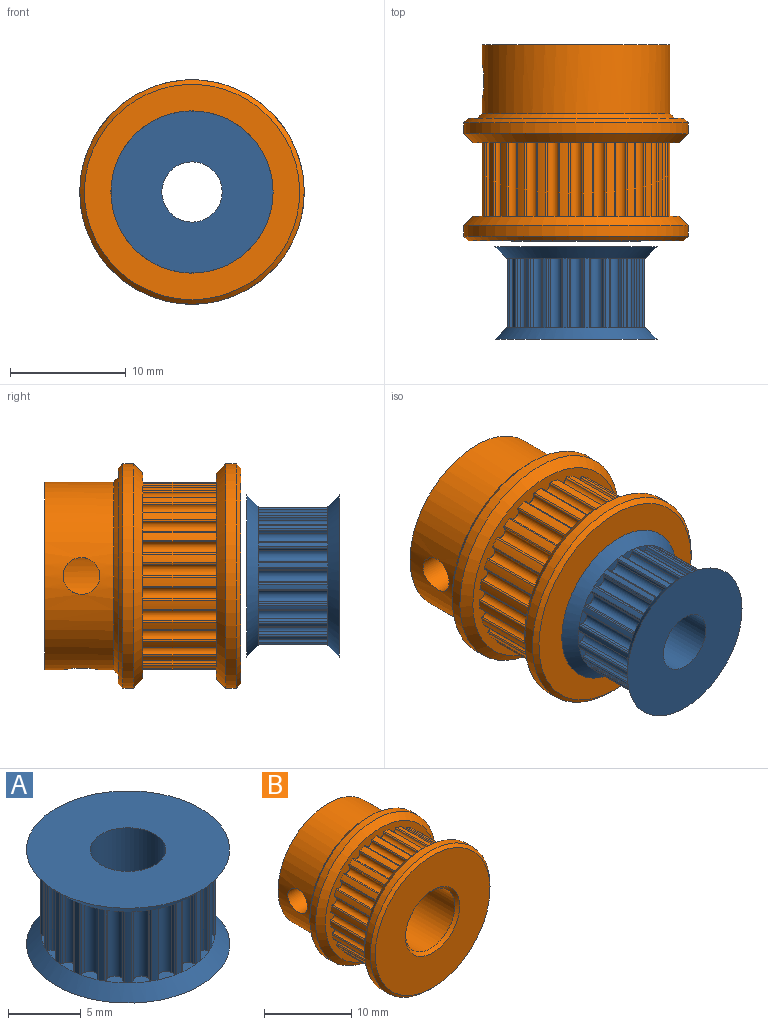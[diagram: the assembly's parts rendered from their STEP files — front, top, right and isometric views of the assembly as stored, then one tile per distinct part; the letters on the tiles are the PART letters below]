
ASSEMBLY  parts=2 mates=1
PART A: 165 faces, bbox 14x14x8 mm
  f0: plane 1.37x0.92mm, normal (0,0,1), area 0.7mm2, adj f65,f66,f67,f68,f69,f164
  f1: plane 1.44x0.75mm, normal (0,0,1), area 0.7mm2, adj f71,f72,f73,f74,f75,f164
  f2: plane 1.37x0.92mm, normal (0,0,1), area 0.7mm2, adj f77,f78,f79,f80,f81,f164
  f3: plane 1.23x1.1mm, normal (0,0,1), area 0.7mm2, adj f83,f84,f85,f86,f87,f164
  f4: plane 1.23x1.1mm, normal (0,0,1), area 0.7mm2, adj f89,f90,f91,f92,f93,f164
  f5: plane 1.37x0.92mm, normal (0,0,1), area 0.7mm2, adj f95,f96,f97,f98,f99,f164
  f6: plane 1.44x0.75mm, normal (0,0,1), area 0.7mm2, adj f101,f102,f103,f104,f105,f164
  f7: plane 1.37x0.92mm, normal (0,0,1), area 0.7mm2, adj f107,f108,f109,f110,f111,f164
  f8: plane 1.23x1.1mm, normal (0,0,1), area 0.7mm2, adj f113,f114,f115,f116,f117,f164
  f9: plane 1.23x1.1mm, normal (0,0,1), area 0.7mm2, adj f119,f120,f121,f122,f123,f164
  f10: plane 1.37x0.92mm, normal (0,0,1), area 0.7mm2, adj f125,f126,f127,f128,f129,f164
  f11: plane 1.44x0.75mm, normal (0,0,1), area 0.7mm2, adj f131,f132,f133,f134,f135,f164
  f12: plane 1.37x0.92mm, normal (0,0,1), area 0.7mm2, adj f137,f138,f139,f140,f141,f164
  f13: plane 1.23x1.1mm, normal (0,0,1), area 0.7mm2, adj f143,f144,f145,f146,f147,f164
  f14: plane 1.23x1.1mm, normal (0,0,1), area 0.7mm2, adj f149,f150,f151,f152,f153,f164
  f15: plane 1.37x0.92mm, normal (0,0,1), area 0.7mm2, adj f38,f39,f155,f156,f157,f164
  f16: plane 1.44x0.75mm, normal (0,0,1), area 0.7mm2, adj f41,f42,f43,f44,f45,f164
  f17: plane 1.37x0.92mm, normal (0,0,1), area 0.7mm2, adj f47,f48,f49,f50,f51,f164
  f18: plane 1.23x1.1mm, normal (0,0,1), area 0.7mm2, adj f53,f54,f55,f56,f57,f164
  f19: plane 1.23x1.1mm, normal (0,0,-1), area 0.7mm2, adj f59,f60,f61,f62,f63,f163
  f20: plane 1.23x1.1mm, normal (0,0,-1), area 0.7mm2, adj f53,f54,f55,f56,f57,f163
  f21: plane 1.37x0.92mm, normal (0,0,-1), area 0.7mm2, adj f47,f48,f49,f50,f51,f163
  f22: plane 1.44x0.75mm, normal (0,0,-1), area 0.7mm2, adj f41,f42,f43,f44,f45,f163
  f23: plane 1.37x0.92mm, normal (0,0,-1), area 0.7mm2, adj f38,f39,f155,f156,f157,f163
  f24: plane 1.23x1.1mm, normal (0,0,-1), area 0.7mm2, adj f149,f150,f151,f152,f153,f163
  f25: plane 1.23x1.1mm, normal (0,0,-1), area 0.7mm2, adj f143,f144,f145,f146,f147,f163
  f26: plane 1.37x0.92mm, normal (0,0,-1), area 0.7mm2, adj f137,f138,f139,f140,f141,f163
  f27: plane 1.44x0.75mm, normal (0,0,-1), area 0.7mm2, adj f131,f132,f133,f134,f135,f163
  f28: plane 1.37x0.92mm, normal (0,0,-1), area 0.7mm2, adj f125,f126,f127,f128,f129,f163
  f29: plane 1.23x1.1mm, normal (0,0,-1), area 0.7mm2, adj f119,f120,f121,f122,f123,f163
  f30: plane 1.23x1.1mm, normal (0,0,-1), area 0.7mm2, adj f113,f114,f115,f116,f117,f163
  f31: plane 1.37x0.92mm, normal (0,0,-1), area 0.7mm2, adj f107,f108,f109,f110,f111,f163
  f32: plane 1.44x0.75mm, normal (0,0,-1), area 0.7mm2, adj f101,f102,f103,f104,f105,f163
  f33: plane 1.37x0.92mm, normal (0,0,-1), area 0.7mm2, adj f95,f96,f97,f98,f99,f163
  f34: plane 1.23x1.1mm, normal (0,0,-1), area 0.7mm2, adj f89,f90,f91,f92,f93,f163
  f35: plane 1.23x1.1mm, normal (0,0,-1), area 0.7mm2, adj f83,f84,f85,f86,f87,f163
  f36: plane 1.37x0.92mm, normal (0,0,-1), area 0.7mm2, adj f77,f78,f79,f80,f81,f163
  f37: plane 1.44x0.75mm, normal (0,0,-1), area 0.7mm2, adj f71,f72,f73,f74,f75,f163
  f38: cylinder r=1mm len=6mm, axis (0,0,-1), area 1.5mm2, adj f15,f23,f39,f157
  f39: cylinder r=0.15mm len=6mm, axis (0,0,-1), area 1.1mm2, adj f15,f23,f38,f40
  f40: cylinder r=6mm len=6mm, axis (0,0,-1), area 2.7mm2, adj f39,f41,f163,f164
  f41: cylinder r=0.15mm len=6mm, axis (0,0,-1), area 1.1mm2, adj f16,f22,f40,f42
  f42: cylinder r=1mm len=6mm, axis (0,0,-1), area 1.5mm2, adj f16,f22,f41,f43
  f43: cylinder r=0.56mm len=6mm, axis (0,0,-1), area 7.9mm2, adj f16,f22,f42,f44
  f44: cylinder r=1mm len=6mm, axis (0,0,-1), area 1.5mm2, adj f16,f22,f43,f45
  f45: cylinder r=0.15mm len=6mm, axis (0,0,-1), area 1.1mm2, adj f16,f22,f44,f46
  f46: cylinder r=6mm len=6mm, axis (0,0,-1), area 2.7mm2, adj f45,f47,f163,f164
  f47: cylinder r=0.15mm len=6mm, axis (0,0,-1), area 1.1mm2, adj f17,f21,f46,f48
  f48: cylinder r=1mm len=6mm, axis (0,0,-1), area 1.5mm2, adj f17,f21,f47,f49
  f49: cylinder r=0.56mm len=6mm, axis (0,0,-1), area 7.9mm2, adj f17,f21,f48,f50
  f50: cylinder r=1mm len=6mm, axis (0,0,-1), area 1.5mm2, adj f17,f21,f49,f51
  f51: cylinder r=0.15mm len=6mm, axis (0,0,-1), area 1.1mm2, adj f17,f21,f50,f52
  f52: cylinder r=6mm len=6mm, axis (0,0,-1), area 2.7mm2, adj f51,f53,f163,f164
  f53: cylinder r=0.15mm len=6mm, axis (0,0,-1), area 1.1mm2, adj f18,f20,f52,f54
  f54: cylinder r=1mm len=6mm, axis (0,0,-1), area 1.5mm2, adj f18,f20,f53,f55
  f55: cylinder r=0.56mm len=6mm, axis (0,0,-1), area 7.9mm2, adj f18,f20,f54,f56
  f56: cylinder r=1mm len=6mm, axis (0,0,-1), area 1.5mm2, adj f18,f20,f55,f57
  f57: cylinder r=0.15mm len=6mm, axis (0,0,-1), area 1.1mm2, adj f18,f20,f56,f58
  f58: cylinder r=6mm len=6mm, axis (0,0,-1), area 2.7mm2, adj f57,f59,f163,f164
  f59: cylinder r=0.15mm len=6mm, axis (0,0,-1), area 1.1mm2, adj f19,f58,f60,f160
  f60: cylinder r=1mm len=6mm, axis (0,0,-1), area 1.5mm2, adj f19,f59,f61,f160
  f61: cylinder r=0.56mm len=6mm, axis (0,0,-1), area 7.9mm2, adj f19,f60,f62,f160
  f62: cylinder r=1mm len=6mm, axis (0,0,-1), area 1.5mm2, adj f19,f61,f63,f160
  f63: cylinder r=0.15mm len=6mm, axis (0,0,-1), area 1.1mm2, adj f19,f62,f64,f160
  f64: cylinder r=6mm len=6mm, axis (0,0,-1), area 2.2mm2, adj f63,f65,f163,f164
  f65: cylinder r=0.15mm len=6mm, axis (0,0,-1), area 1.6mm2, adj f0,f64,f66,f158,f163,f164
  f66: cylinder r=1mm len=6mm, axis (0,0,-1), area 1.5mm2, adj f0,f65,f67,f158
  f67: cylinder r=0.56mm len=6mm, axis (0,0,-1), area 7.9mm2, adj f0,f66,f68,f158
  f68: cylinder r=1mm len=6mm, axis (0,0,-1), area 1.5mm2, adj f0,f67,f69,f158
  f69: cylinder r=0.15mm len=6mm, axis (0,0,-1), area 1.1mm2, adj f0,f68,f70,f158
  f70: cylinder r=6mm len=6mm, axis (0,0,-1), area 2.7mm2, adj f69,f71,f163,f164
  f71: cylinder r=0.15mm len=6mm, axis (0,0,-1), area 1.1mm2, adj f1,f37,f70,f72
  f72: cylinder r=1mm len=6mm, axis (0,0,-1), area 1.5mm2, adj f1,f37,f71,f73
  f73: cylinder r=0.56mm len=6mm, axis (0,0,-1), area 7.9mm2, adj f1,f37,f72,f74
  f74: cylinder r=1mm len=6mm, axis (0,0,-1), area 1.5mm2, adj f1,f37,f73,f75
  f75: cylinder r=0.15mm len=6mm, axis (0,0,-1), area 1.1mm2, adj f1,f37,f74,f76
  f76: cylinder r=6mm len=6mm, axis (0,0,-1), area 2.7mm2, adj f75,f77,f163,f164
  f77: cylinder r=0.15mm len=6mm, axis (0,0,-1), area 1.1mm2, adj f2,f36,f76,f78
  f78: cylinder r=1mm len=6mm, axis (0,0,-1), area 1.5mm2, adj f2,f36,f77,f79
  f79: cylinder r=0.56mm len=6mm, axis (0,0,-1), area 7.9mm2, adj f2,f36,f78,f80
  f80: cylinder r=1mm len=6mm, axis (0,0,-1), area 1.5mm2, adj f2,f36,f79,f81
  f81: cylinder r=0.15mm len=6mm, axis (0,0,-1), area 1.1mm2, adj f2,f36,f80,f82
  f82: cylinder r=6mm len=6mm, axis (0,0,-1), area 2.7mm2, adj f81,f83,f163,f164
  f83: cylinder r=0.15mm len=6mm, axis (0,0,-1), area 1.1mm2, adj f3,f35,f82,f84
  f84: cylinder r=1mm len=6mm, axis (0,0,-1), area 1.5mm2, adj f3,f35,f83,f85
  f85: cylinder r=0.56mm len=6mm, axis (0,0,-1), area 7.9mm2, adj f3,f35,f84,f86
  f86: cylinder r=1mm len=6mm, axis (0,0,-1), area 1.5mm2, adj f3,f35,f85,f87
  f87: cylinder r=0.15mm len=6mm, axis (0,0,-1), area 1.1mm2, adj f3,f35,f86,f88
  f88: cylinder r=6mm len=6mm, axis (0,0,-1), area 2.7mm2, adj f87,f89,f163,f164
  f89: cylinder r=0.15mm len=6mm, axis (0,0,-1), area 1.1mm2, adj f4,f34,f88,f90
  f90: cylinder r=1mm len=6mm, axis (0,0,-1), area 1.5mm2, adj f4,f34,f89,f91
  f91: cylinder r=0.56mm len=6mm, axis (0,0,-1), area 7.9mm2, adj f4,f34,f90,f92
  f92: cylinder r=1mm len=6mm, axis (0,0,-1), area 1.5mm2, adj f4,f34,f91,f93
  f93: cylinder r=0.15mm len=6mm, axis (0,0,-1), area 1.1mm2, adj f4,f34,f92,f94
  f94: cylinder r=6mm len=6mm, axis (0,0,-1), area 2.7mm2, adj f93,f95,f163,f164
  f95: cylinder r=0.15mm len=6mm, axis (0,0,-1), area 1.1mm2, adj f5,f33,f94,f96
  f96: cylinder r=1mm len=6mm, axis (0,0,-1), area 1.5mm2, adj f5,f33,f95,f97
  f97: cylinder r=0.56mm len=6mm, axis (0,0,-1), area 7.9mm2, adj f5,f33,f96,f98
  f98: cylinder r=1mm len=6mm, axis (0,0,-1), area 1.5mm2, adj f5,f33,f97,f99
  f99: cylinder r=0.15mm len=6mm, axis (0,0,-1), area 1.1mm2, adj f5,f33,f98,f100
  f100: cylinder r=6mm len=6mm, axis (0,0,-1), area 2.7mm2, adj f99,f101,f163,f164
  f101: cylinder r=0.15mm len=6mm, axis (0,0,-1), area 1.1mm2, adj f6,f32,f100,f102
  f102: cylinder r=1mm len=6mm, axis (0,0,-1), area 1.5mm2, adj f6,f32,f101,f103
  f103: cylinder r=0.56mm len=6mm, axis (0,0,-1), area 7.9mm2, adj f6,f32,f102,f104
  f104: cylinder r=1mm len=6mm, axis (0,0,-1), area 1.5mm2, adj f6,f32,f103,f105
  f105: cylinder r=0.15mm len=6mm, axis (0,0,-1), area 1.1mm2, adj f6,f32,f104,f106
  f106: cylinder r=6mm len=6mm, axis (0,0,-1), area 2.7mm2, adj f105,f107,f163,f164
  f107: cylinder r=0.15mm len=6mm, axis (0,0,-1), area 1.1mm2, adj f7,f31,f106,f108
  f108: cylinder r=1mm len=6mm, axis (0,0,-1), area 1.5mm2, adj f7,f31,f107,f109
  f109: cylinder r=0.56mm len=6mm, axis (0,0,-1), area 7.9mm2, adj f7,f31,f108,f110
  f110: cylinder r=1mm len=6mm, axis (0,0,-1), area 1.5mm2, adj f7,f31,f109,f111
  f111: cylinder r=0.15mm len=6mm, axis (0,0,-1), area 1.1mm2, adj f7,f31,f110,f112
  f112: cylinder r=6mm len=6mm, axis (0,0,-1), area 2.7mm2, adj f111,f113,f163,f164
  f113: cylinder r=0.15mm len=6mm, axis (0,0,-1), area 1.1mm2, adj f8,f30,f112,f114
  f114: cylinder r=1mm len=6mm, axis (0,0,-1), area 1.5mm2, adj f8,f30,f113,f115
  f115: cylinder r=0.56mm len=6mm, axis (0,0,-1), area 7.9mm2, adj f8,f30,f114,f116
  f116: cylinder r=1mm len=6mm, axis (0,0,-1), area 1.5mm2, adj f8,f30,f115,f117
  f117: cylinder r=0.15mm len=6mm, axis (0,0,-1), area 1.1mm2, adj f8,f30,f116,f118
  f118: cylinder r=6mm len=6mm, axis (0,0,-1), area 2.7mm2, adj f117,f119,f163,f164
  f119: cylinder r=0.15mm len=6mm, axis (0,0,-1), area 1.1mm2, adj f9,f29,f118,f120
  f120: cylinder r=1mm len=6mm, axis (0,0,-1), area 1.5mm2, adj f9,f29,f119,f121
  f121: cylinder r=0.56mm len=6mm, axis (0,0,-1), area 7.9mm2, adj f9,f29,f120,f122
  f122: cylinder r=1mm len=6mm, axis (0,0,-1), area 1.5mm2, adj f9,f29,f121,f123
  f123: cylinder r=0.15mm len=6mm, axis (0,0,-1), area 1.1mm2, adj f9,f29,f122,f124
  f124: cylinder r=6mm len=6mm, axis (0,0,-1), area 2.7mm2, adj f123,f125,f163,f164
  f125: cylinder r=0.15mm len=6mm, axis (0,0,-1), area 1.1mm2, adj f10,f28,f124,f126
  f126: cylinder r=1mm len=6mm, axis (0,0,-1), area 1.5mm2, adj f10,f28,f125,f127
  f127: cylinder r=0.56mm len=6mm, axis (0,0,-1), area 7.9mm2, adj f10,f28,f126,f128
  f128: cylinder r=1mm len=6mm, axis (0,0,-1), area 1.5mm2, adj f10,f28,f127,f129
  f129: cylinder r=0.15mm len=6mm, axis (0,0,-1), area 1.1mm2, adj f10,f28,f128,f130
  f130: cylinder r=6mm len=6mm, axis (0,0,-1), area 2.7mm2, adj f129,f131,f163,f164
  f131: cylinder r=0.15mm len=6mm, axis (0,0,-1), area 1.1mm2, adj f11,f27,f130,f132
  f132: cylinder r=1mm len=6mm, axis (0,0,-1), area 1.5mm2, adj f11,f27,f131,f133
  f133: cylinder r=0.56mm len=6mm, axis (0,0,-1), area 7.9mm2, adj f11,f27,f132,f134
  f134: cylinder r=1mm len=6mm, axis (0,0,-1), area 1.5mm2, adj f11,f27,f133,f135
  f135: cylinder r=0.15mm len=6mm, axis (0,0,-1), area 1.1mm2, adj f11,f27,f134,f136
  f136: cylinder r=6mm len=6mm, axis (0,0,-1), area 2.7mm2, adj f135,f137,f163,f164
  f137: cylinder r=0.15mm len=6mm, axis (0,0,-1), area 1.1mm2, adj f12,f26,f136,f138
  f138: cylinder r=1mm len=6mm, axis (0,0,-1), area 1.5mm2, adj f12,f26,f137,f139
  f139: cylinder r=0.56mm len=6mm, axis (0,0,-1), area 7.9mm2, adj f12,f26,f138,f140
  f140: cylinder r=1mm len=6mm, axis (0,0,-1), area 1.5mm2, adj f12,f26,f139,f141
  f141: cylinder r=0.15mm len=6mm, axis (0,0,-1), area 1.1mm2, adj f12,f26,f140,f142
  f142: cylinder r=6mm len=6mm, axis (0,0,-1), area 2.7mm2, adj f141,f143,f163,f164
  f143: cylinder r=0.15mm len=6mm, axis (0,0,-1), area 1.1mm2, adj f13,f25,f142,f144
  f144: cylinder r=1mm len=6mm, axis (0,0,-1), area 1.5mm2, adj f13,f25,f143,f145
  f145: cylinder r=0.56mm len=6mm, axis (0,0,-1), area 7.9mm2, adj f13,f25,f144,f146
  f146: cylinder r=1mm len=6mm, axis (0,0,-1), area 1.5mm2, adj f13,f25,f145,f147
  f147: cylinder r=0.15mm len=6mm, axis (0,0,-1), area 1.1mm2, adj f13,f25,f146,f148
  f148: cylinder r=6mm len=6mm, axis (0,0,-1), area 2.7mm2, adj f147,f149,f163,f164
  f149: cylinder r=0.15mm len=6mm, axis (0,0,-1), area 1.1mm2, adj f14,f24,f148,f150
  f150: cylinder r=1mm len=6mm, axis (0,0,-1), area 1.5mm2, adj f14,f24,f149,f151
  f151: cylinder r=0.56mm len=6mm, axis (0,0,-1), area 7.9mm2, adj f14,f24,f150,f152
  f152: cylinder r=1mm len=6mm, axis (0,0,-1), area 1.5mm2, adj f14,f24,f151,f153
  f153: cylinder r=0.15mm len=6mm, axis (0,0,-1), area 1.1mm2, adj f14,f24,f152,f154
  f154: cylinder r=6mm len=6mm, axis (0,0,-1), area 2.7mm2, adj f153,f155,f163,f164
  f155: cylinder r=0.15mm len=6mm, axis (0,0,-1), area 1.1mm2, adj f15,f23,f154,f156
  f156: cylinder r=1mm len=6mm, axis (0,0,-1), area 1.5mm2, adj f15,f23,f155,f157
  f157: cylinder r=0.56mm len=6mm, axis (0,0,-1), area 7.9mm2, adj f15,f23,f38,f156
  f158: plane 1.37x0.92mm, normal (0,0,-1), area 0.7mm2, adj f65,f66,f67,f68,f69,f163
  f159: plane 14x14mm, normal (0,0,1), area 132.7mm2, adj f162,f163
  f160: plane 1.23x1.1mm, normal (0,0,1), area 0.7mm2, adj f59,f60,f61,f62,f63,f164
  f161: plane 14x14mm, normal (0,0,-1), area 132.7mm2, adj f162,f164
  f162: cylinder r=2.6mm len=8mm, axis (0,0,-1), area 130.7mm2, adj f159,f161
  f163: cone r=7mm half-angle=45deg, axis (0,0,1), area 57.8mm2, adj f19,f20,f21,f22,f23,f24,f25,f26
  f164: cone r=7mm half-angle=45deg, axis (0,0,-1), area 57.8mm2, adj f0,f1,f2,f3,f4,f5,f6,f7
PART B: 117 faces, bbox 19.4x16.9x19.4 mm
  f0: cylinder r=8.1mm len=16.21mm, axis (0,-1,0), area 287.2mm2, adj f1,f108,f114,f116
  f1: cylinder r=1.59mm len=4.43mm, axis (1,0,0), area 41.8mm2, adj f0,f109
  f2: cylinder r=0.5mm len=6.35mm, axis (0,1,0), area 9.8mm2, adj f3,f101,f102,f105
  f3: cylinder r=0.12mm len=6.35mm, axis (0,1,0), area 1.3mm2, adj f2,f4,f102,f105
  f4: cylinder r=8.1mm len=6.35mm, axis (0,1,0), area 4.9mm2, adj f3,f5,f102,f105
  f5: cylinder r=0.12mm len=6.35mm, axis (0,1,0), area 1.3mm2, adj f4,f6,f102,f105
  f6: cylinder r=0.5mm len=6.35mm, axis (0,1,0), area 9.8mm2, adj f5,f7,f102,f105
  f7: cylinder r=0.12mm len=6.35mm, axis (0,1,0), area 1.3mm2, adj f6,f8,f102,f105
  f8: cylinder r=8.1mm len=6.35mm, axis (0,1,0), area 4.9mm2, adj f7,f9,f102,f105
  f9: cylinder r=0.12mm len=6.35mm, axis (0,1,0), area 1.3mm2, adj f8,f10,f102,f105
  f10: cylinder r=0.5mm len=6.35mm, axis (0,1,0), area 9.8mm2, adj f9,f11,f102,f105
  f11: cylinder r=0.12mm len=6.35mm, axis (0,1,0), area 1.3mm2, adj f10,f12,f102,f105
  f12: cylinder r=8.1mm len=6.35mm, axis (0,1,0), area 4.9mm2, adj f11,f13,f102,f105
  f13: cylinder r=0.12mm len=6.35mm, axis (0,1,0), area 1.3mm2, adj f12,f14,f102,f105
  f14: cylinder r=0.5mm len=6.35mm, axis (0,1,0), area 9.8mm2, adj f13,f15,f102,f105
  f15: cylinder r=0.12mm len=6.35mm, axis (0,1,0), area 1.3mm2, adj f14,f16,f102,f105
  f16: cylinder r=8.1mm len=6.35mm, axis (0,1,0), area 4.9mm2, adj f15,f17,f102,f105
  f17: cylinder r=0.12mm len=6.35mm, axis (0,1,0), area 1.3mm2, adj f16,f18,f102,f105
  f18: cylinder r=0.5mm len=6.35mm, axis (0,1,0), area 9.8mm2, adj f17,f19,f102,f105
  f19: cylinder r=0.12mm len=6.35mm, axis (0,1,0), area 1.3mm2, adj f18,f20,f102,f105
  f20: cylinder r=8.1mm len=6.35mm, axis (0,1,0), area 4.9mm2, adj f19,f21,f102,f105
  f21: cylinder r=0.12mm len=6.35mm, axis (0,1,0), area 1.3mm2, adj f20,f22,f102,f105
  f22: cylinder r=0.5mm len=6.35mm, axis (0,1,0), area 9.8mm2, adj f21,f23,f102,f105
  f23: cylinder r=0.12mm len=6.35mm, axis (0,1,0), area 1.3mm2, adj f22,f24,f102,f105
  f24: cylinder r=8.1mm len=6.35mm, axis (0,1,0), area 4.9mm2, adj f23,f25,f102,f105
  f25: cylinder r=0.12mm len=6.35mm, axis (0,1,0), area 1.3mm2, adj f24,f26,f102,f105
  f26: cylinder r=0.5mm len=6.35mm, axis (0,1,0), area 9.8mm2, adj f25,f27,f102,f105
  f27: cylinder r=0.12mm len=6.35mm, axis (0,1,0), area 1.3mm2, adj f26,f28,f102,f105
  f28: cylinder r=8.1mm len=6.35mm, axis (0,1,0), area 4.9mm2, adj f27,f29,f102,f105
  f29: cylinder r=0.12mm len=6.35mm, axis (0,1,0), area 1.3mm2, adj f28,f30,f102,f105
  f30: cylinder r=0.5mm len=6.35mm, axis (0,1,0), area 9.8mm2, adj f29,f31,f102,f105
  f31: cylinder r=0.12mm len=6.35mm, axis (0,1,0), area 1.3mm2, adj f30,f32,f102,f105
  f32: cylinder r=8.1mm len=6.35mm, axis (0,1,0), area 4.9mm2, adj f31,f33,f102,f105
  f33: cylinder r=0.12mm len=6.35mm, axis (0,1,0), area 1.3mm2, adj f32,f34,f102,f105
  f34: cylinder r=0.5mm len=6.35mm, axis (0,1,0), area 9.8mm2, adj f33,f35,f102,f105
  f35: cylinder r=0.12mm len=6.35mm, axis (0,1,0), area 1.3mm2, adj f34,f36,f102,f105
  f36: cylinder r=8.1mm len=6.35mm, axis (0,1,0), area 4.9mm2, adj f35,f37,f102,f105
  f37: cylinder r=0.12mm len=6.35mm, axis (0,1,0), area 1.3mm2, adj f36,f38,f102,f105
  f38: cylinder r=0.5mm len=6.35mm, axis (0,1,0), area 9.8mm2, adj f37,f39,f102,f105
  f39: cylinder r=0.12mm len=6.35mm, axis (0,1,0), area 1.3mm2, adj f38,f40,f102,f105
  f40: cylinder r=8.1mm len=6.35mm, axis (0,1,0), area 4.9mm2, adj f39,f41,f102,f105
  f41: cylinder r=0.12mm len=6.35mm, axis (0,1,0), area 1.3mm2, adj f40,f42,f102,f105
  f42: cylinder r=0.5mm len=6.35mm, axis (0,1,0), area 9.8mm2, adj f41,f43,f102,f105
  f43: cylinder r=0.12mm len=6.35mm, axis (0,1,0), area 1.3mm2, adj f42,f44,f102,f105
  f44: cylinder r=8.1mm len=6.35mm, axis (0,1,0), area 4.9mm2, adj f43,f45,f102,f105
  f45: cylinder r=0.12mm len=6.35mm, axis (0,1,0), area 1.3mm2, adj f44,f46,f102,f105
  f46: cylinder r=0.5mm len=6.35mm, axis (0,1,0), area 9.8mm2, adj f45,f47,f102,f105
  f47: cylinder r=0.12mm len=6.35mm, axis (0,1,0), area 1.3mm2, adj f46,f48,f102,f105
  f48: cylinder r=8.1mm len=6.35mm, axis (0,1,0), area 4.9mm2, adj f47,f49,f102,f105
  f49: cylinder r=0.12mm len=6.35mm, axis (0,1,0), area 1.3mm2, adj f48,f50,f102,f105
  f50: cylinder r=0.5mm len=6.35mm, axis (0,1,0), area 9.8mm2, adj f49,f51,f102,f105
  f51: cylinder r=0.12mm len=6.35mm, axis (0,1,0), area 1.3mm2, adj f50,f52,f102,f105
  f52: cylinder r=8.1mm len=6.35mm, axis (0,1,0), area 4.9mm2, adj f51,f53,f102,f105
  f53: cylinder r=0.12mm len=6.35mm, axis (0,1,0), area 1.3mm2, adj f52,f54,f102,f105
  f54: cylinder r=0.5mm len=6.35mm, axis (0,1,0), area 9.8mm2, adj f53,f55,f102,f105
  f55: cylinder r=0.12mm len=6.35mm, axis (0,1,0), area 1.3mm2, adj f54,f56,f102,f105
  f56: cylinder r=8.1mm len=6.35mm, axis (0,1,0), area 4.9mm2, adj f55,f57,f102,f105
  f57: cylinder r=0.12mm len=6.35mm, axis (0,1,0), area 1.3mm2, adj f56,f58,f102,f105
  f58: cylinder r=0.5mm len=6.35mm, axis (0,1,0), area 9.8mm2, adj f57,f59,f102,f105
  f59: cylinder r=0.12mm len=6.35mm, axis (0,1,0), area 1.3mm2, adj f58,f60,f102,f105
  f60: cylinder r=8.1mm len=6.35mm, axis (0,1,0), area 4.9mm2, adj f59,f61,f102,f105
  f61: cylinder r=0.12mm len=6.35mm, axis (0,1,0), area 1.3mm2, adj f60,f62,f102,f105
  f62: cylinder r=0.5mm len=6.35mm, axis (0,1,0), area 9.8mm2, adj f61,f63,f102,f105
  f63: cylinder r=0.12mm len=6.35mm, axis (0,1,0), area 1.3mm2, adj f62,f64,f102,f105
  f64: cylinder r=8.1mm len=6.35mm, axis (0,1,0), area 4.9mm2, adj f63,f65,f102,f105
  f65: cylinder r=0.12mm len=6.35mm, axis (0,1,0), area 1.3mm2, adj f64,f66,f102,f105
  f66: cylinder r=0.5mm len=6.35mm, axis (0,1,0), area 9.8mm2, adj f65,f67,f102,f105
  f67: cylinder r=0.12mm len=6.35mm, axis (0,1,0), area 1.3mm2, adj f66,f68,f102,f105
  f68: cylinder r=8.1mm len=6.35mm, axis (0,1,0), area 4.9mm2, adj f67,f69,f102,f105
  f69: cylinder r=0.12mm len=6.35mm, axis (0,1,0), area 1.3mm2, adj f68,f70,f102,f105
  f70: cylinder r=0.5mm len=6.35mm, axis (0,1,0), area 9.8mm2, adj f69,f71,f102,f105
  f71: cylinder r=0.12mm len=6.35mm, axis (0,1,0), area 1.3mm2, adj f70,f72,f102,f105
  f72: cylinder r=8.1mm len=6.35mm, axis (0,1,0), area 4.9mm2, adj f71,f73,f102,f105
  f73: cylinder r=0.12mm len=6.35mm, axis (0,1,0), area 1.3mm2, adj f72,f74,f102,f105
  f74: cylinder r=0.5mm len=6.35mm, axis (0,1,0), area 9.8mm2, adj f73,f75,f102,f105
  f75: cylinder r=0.12mm len=6.35mm, axis (0,1,0), area 1.3mm2, adj f74,f76,f102,f105
  f76: cylinder r=8.1mm len=6.35mm, axis (0,1,0), area 4.9mm2, adj f75,f77,f102,f105
  f77: cylinder r=0.12mm len=6.35mm, axis (0,1,0), area 1.3mm2, adj f76,f78,f102,f105
  f78: cylinder r=0.5mm len=6.35mm, axis (0,1,0), area 9.8mm2, adj f77,f79,f102,f105
  f79: cylinder r=0.12mm len=6.35mm, axis (0,1,0), area 1.3mm2, adj f78,f80,f102,f105
  f80: cylinder r=8.1mm len=6.35mm, axis (0,1,0), area 4.9mm2, adj f79,f81,f102,f105
  f81: cylinder r=0.12mm len=6.35mm, axis (0,1,0), area 1.3mm2, adj f80,f82,f102,f105
  f82: cylinder r=0.5mm len=6.35mm, axis (0,1,0), area 9.8mm2, adj f81,f83,f102,f105
  f83: cylinder r=0.12mm len=6.35mm, axis (0,1,0), area 1.3mm2, adj f82,f84,f102,f105
  f84: cylinder r=8.1mm len=6.35mm, axis (0,1,0), area 4.9mm2, adj f83,f85,f102,f105
  f85: cylinder r=0.12mm len=6.35mm, axis (0,1,0), area 1.3mm2, adj f84,f86,f102,f105
  f86: cylinder r=0.5mm len=6.35mm, axis (0,1,0), area 9.8mm2, adj f85,f87,f102,f105
  f87: cylinder r=0.12mm len=6.35mm, axis (0,1,0), area 1.3mm2, adj f86,f88,f102,f105
  f88: cylinder r=8.1mm len=6.35mm, axis (0,1,0), area 4.9mm2, adj f87,f89,f102,f105
  f89: cylinder r=0.12mm len=6.35mm, axis (0,1,0), area 1.3mm2, adj f88,f90,f102,f105
  f90: cylinder r=0.5mm len=6.35mm, axis (0,1,0), area 9.8mm2, adj f89,f91,f102,f105
  f91: cylinder r=0.12mm len=6.35mm, axis (0,1,0), area 1.3mm2, adj f90,f92,f102,f105
  f92: cylinder r=8.1mm len=6.35mm, axis (0,1,0), area 4.9mm2, adj f91,f93,f102,f105
  f93: cylinder r=0.12mm len=6.35mm, axis (0,1,0), area 1.3mm2, adj f92,f94,f102,f105
  f94: cylinder r=0.5mm len=6.35mm, axis (0,1,0), area 9.8mm2, adj f93,f95,f102,f105
  f95: cylinder r=0.12mm len=6.35mm, axis (0,1,0), area 1.3mm2, adj f94,f96,f102,f105
  f96: cylinder r=8.1mm len=6.35mm, axis (0,1,0), area 4.9mm2, adj f95,f97,f102,f105
  f97: cylinder r=0.12mm len=6.35mm, axis (0,1,0), area 1.3mm2, adj f96,f98,f102,f105
  f98: cylinder r=0.5mm len=6.35mm, axis (0,1,0), area 9.8mm2, adj f97,f99,f102,f105
  f99: cylinder r=0.12mm len=6.35mm, axis (0,1,0), area 1.3mm2, adj f98,f100,f102,f105
  f100: cylinder r=8.1mm len=6.35mm, axis (0,1,0), area 4.9mm2, adj f99,f101,f102,f105
  f101: cylinder r=0.12mm len=6.35mm, axis (0,1,0), area 1.3mm2, adj f2,f100,f102,f105
  f102: plane 17.8x17.8mm, normal (0,-1,0), area 55.4mm2, adj f2,f3,f4,f5,f6,f7,f8,f9
  f103: cylinder r=9.69mm len=19.38mm, axis (0,-1,0), area 56.4mm2, adj f110,f115
  f104: plane 18.59x18.59mm, normal (0,1,0), area 44.4mm2, adj f114,f115
  f105: plane 17.8x17.8mm, normal (0,1,0), area 55.4mm2, adj f2,f3,f4,f5,f6,f7,f8,f9
  f106: cylinder r=9.69mm len=19.38mm, axis (0,1,0), area 56.4mm2, adj f111,f113
  f107: plane 18.59x18.59mm, normal (0,-1,0), area 210.7mm2, adj f112,f113
  f108: plane 16.21x16.21mm, normal (0,1,0), area 156mm2, adj f0,f109
  f109: cylinder r=4mm len=16.54mm, axis (0,1,0), area 399.4mm2, adj f1,f108,f112,f116
  f110: cone r=9.69mm half-angle=45deg, axis (0,1,0), area 65.6mm2, adj f102,f103
  f111: cone r=9.69mm half-angle=45deg, axis (0,-1,0), area 65.6mm2, adj f105,f106
  f112: cone r=4.4mm half-angle=45deg, axis (0,-1,0), area 14.8mm2, adj f107,f109
  f113: cone r=9.29mm half-angle=45deg, axis (0,1,0), area 33.5mm2, adj f106,f107
  f114: cone r=8.1mm half-angle=45deg, axis (0,-1,0), area 29.3mm2, adj f0,f104
  f115: cone r=9.29mm half-angle=45deg, axis (0,-1,0), area 33.5mm2, adj f103,f104
  f116: cylinder r=1.59mm len=4.43mm, axis (0,0,1), area 41.8mm2, adj f0,f109
PLACE A rot(axis=(1,0,0),90deg) t=(-15.23,-25.54,4.22)mm
PLACE B t=(-15.23,-15.57,4.22)mm
MATE parallel A.f40 <-> B.f0  axis (0,1,0) through (-15.23,-24.54,4.22)mm
